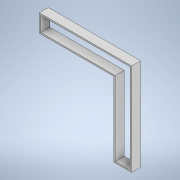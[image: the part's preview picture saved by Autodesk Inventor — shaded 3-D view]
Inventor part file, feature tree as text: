
AUTODESK INVENTOR PART (.ipt)
format: ipt  version: 2022 (Build 260153000, 153)  size: 114,688 bytes
history: native  units: mm
features: other x1, extrude x1, sketch x1
ambient origin geometry x8: Origin, YZ Plane, XZ Plane, XY Plane, X Axis, Y Axis, Z Axis, Center Point
bodies: Body1 (feature_tree)
feature tree (3):
  other  "솔리드1"
  extrude  "돌출1"  Depth=5.0mm
  sketch  "스케치1"
